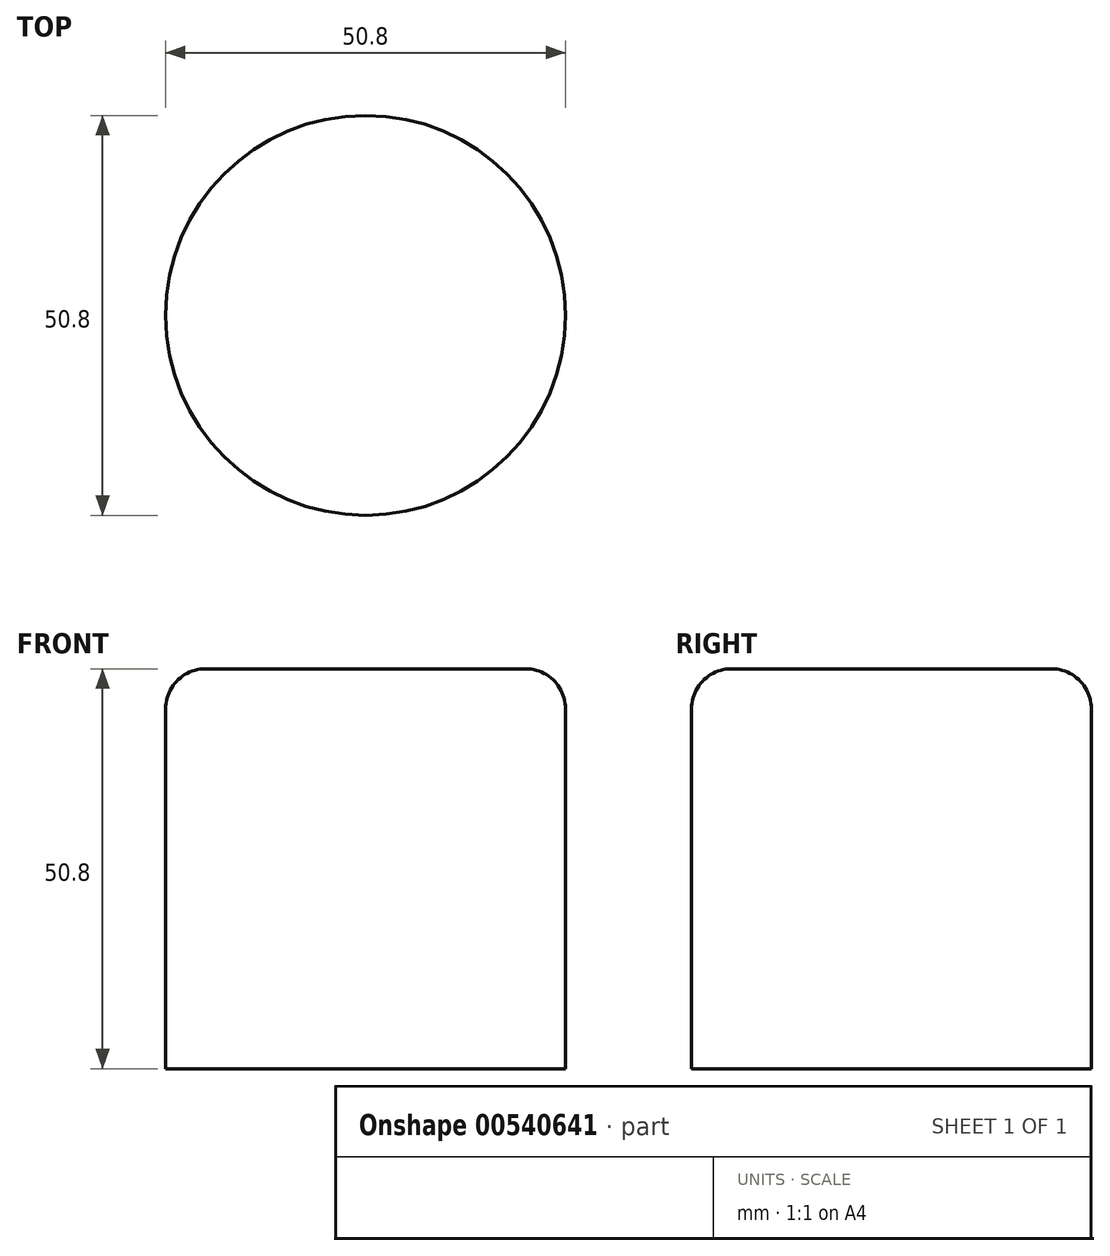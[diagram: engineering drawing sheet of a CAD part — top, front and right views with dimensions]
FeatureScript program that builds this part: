
annotation { "Feature Type Name" : "Feature", "Feature Type Description" : "" }
export const myFeature = defineFeature(function(context is Context, id is Id, definition is map)
    precondition{}
    {
        {
            var Q0;
            Q0=qCreatedBy(makeId("Top.planeOp"),FACE);
            var sketch = newSketch(context, id + "F0", { "sketchPlane" : qUnion([Q0])});
            skCircle(sketch, "E0", {"center": v(0, 0) * mm, "radius": 25.4 * mm});
            skSolve(sketch);
        }
        {
            var Q0;
            Q0=qCreatedBy(makeId("Top.planeOp"),FACE);
            cPlane(context, id + "F1", {"entities" : qUnion([Q0]), "cplaneType" : CPlaneType.OFFSET, "offset" : 50.8 * mm, "width" : 152.4 * mm, "height" : 152.4 * mm});
        }
        {
            var Q0;
            Q0=qCreatedBy(id+"F1.planeOp",FACE);
            cPlane(context, id + "F2", {"entities" : qUnion([Q0]), "cplaneType" : CPlaneType.OFFSET, "offset" : 101.6 * mm, "width" : 152.4 * mm, "height" : 152.4 * mm});
        }
        {
            var Q0;
            Q0=makeQuery(id+"F0.imprint","IMPRINT",FACE,{"disambiguationData":[TD([[makeQuery(id+"F0.imprint","IMPRINT",EDGE,{"derivedFrom":sQuery(id+"F0.wireOp",EDGE,"E0")}),1.0]])]});
            extrude(context, id + "F3", {"entities" : qUnion([Q0]), "depth" : 50.8 * mm, "offsetDistance" : 25.4 * mm});
        }
        {
            var Q0;
            Q0=makeQuery(id+"F3.opExtrude","CAP_EDGE",EDGE,{"disambiguationData":[OSD([sQuery(id+"F0.wireOp",EDGE,"E0")])],"isStart":false});
            fillet(context, id + "F4", {"entities" : qUnion([Q0]), "radius" : 5.08 * mm, "tangentPropagation" : true, "allowEdgeOverflow" : false});
        }
    });
